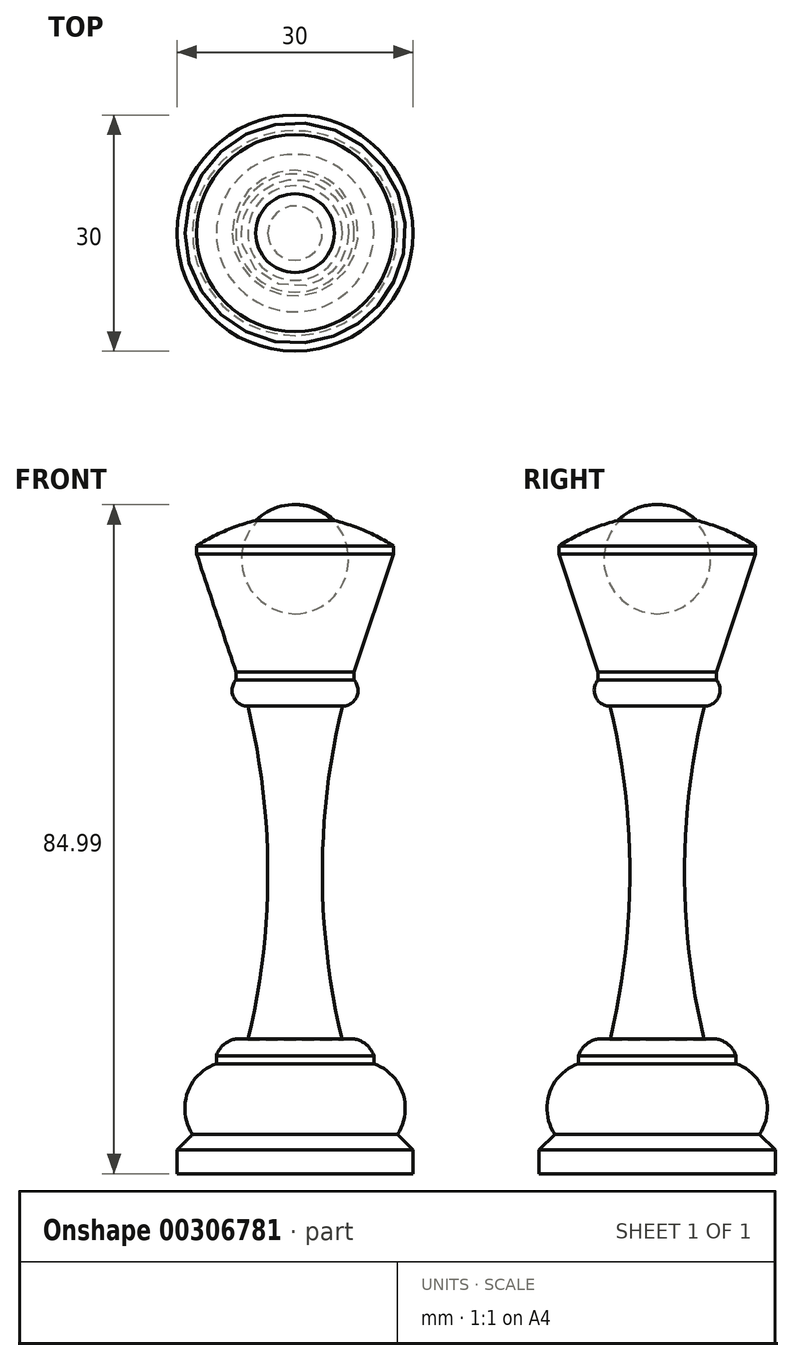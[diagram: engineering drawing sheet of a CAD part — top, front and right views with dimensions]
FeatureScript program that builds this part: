
annotation { "Feature Type Name" : "Feature", "Feature Type Description" : "" }
export const myFeature = defineFeature(function(context is Context, id is Id, definition is map)
    precondition{}
    {
        {
            var Q0;
            Q0=qCreatedBy(makeId("Front.planeOp"),FACE);
            var sketch = newSketch(context, id + "F0", { "sketchPlane" : qUnion([Q0])});
            skArc(sketch, "E0", {"start": v(12.5, -5.27) * mm, "mid": v(8.88, -3.33) * mm, "end": v(5, -2) * mm});
            skLineSegment(sketch, "E1", {"start": v(12.5, -5.27) * mm, "end": v(12.5, -6.27) * mm});
            skArc(sketch, "E2", {"start": v(6, -25.6) * mm, "mid": v(7.82, -24.41) * mm, "end": v(7.5, -22.27) * mm});
            skArc(sketch, "E3", {"start": v(6, -25.6) * mm, "mid": v(3.46, -46.8) * mm, "end": v(6, -68.02) * mm});
            skArc(sketch, "E4", {"start": v(13, -80) * mm, "mid": v(13.7, -74.77) * mm, "end": v(10, -71.02) * mm});
            skLineSegment(sketch, "E5", {"start": v(15, -82) * mm, "end": v(13, -80) * mm});
            skLineSegment(sketch, "E6", {"start": v(15, -82) * mm, "end": v(15, -85) * mm});
            skLineSegment(sketch, "E7", {"start": v(15, -84.99) * mm, "end": v(0, -84.99) * mm});
            skLineSegment(sketch, "E8", {"start": v(0, -84.99) * mm, "end": v(0, 0) * mm});
            skLineSegment(sketch, "E9", {"start": v(12.5, -6.27) * mm, "end": v(0, -6.27) * mm});
            skLineSegment(sketch, "E10", {"start": v(12.5, -5.27) * mm, "end": v(0, -5.27) * mm});
            skLineSegment(sketch, "E11", {"start": v(7.5, -22.27) * mm, "end": v(0, -22.27) * mm});
            skArc(sketch, "E12", {"start": v(5, -2) * mm, "mid": v(2.7, -0.5) * mm, "end": v(0, 0) * mm});
            skLineSegment(sketch, "E13", {"start": v(6, -25.6) * mm, "end": v(0, -25.6) * mm});
            skLineSegment(sketch, "E14", {"start": v(6, -68.02) * mm, "end": v(0, -68.02) * mm});
            skLineSegment(sketch, "E15", {"start": v(10, -71.02) * mm, "end": v(0, -71.02) * mm});
            skLineSegment(sketch, "E16", {"start": v(10, -70.02) * mm, "end": v(0, -70.02) * mm});
            skLineSegment(sketch, "E17", {"start": v(13, -79.99) * mm, "end": v(0, -79.99) * mm});
            skLineSegment(sketch, "E18", {"start": v(15, -81.99) * mm, "end": v(0, -81.99) * mm});
            skLineSegment(sketch, "E19", {"start": v(7.5, -21.27) * mm, "end": v(0, -21.27) * mm});
            skLineSegment(sketch, "E20", {"start": v(12.5, -6.27) * mm, "end": v(7.5, -21.27) * mm});
            skLineSegment(sketch, "E21", {"start": v(7.5, -22.27) * mm, "end": v(7.5, -21.27) * mm});
            skLineSegment(sketch, "E22", {"start": v(10, -71.02) * mm, "end": v(10, -70.02) * mm});
            skArc(sketch, "E23", {"start": v(10, -70.02) * mm, "mid": v(8.42, -68.18) * mm, "end": v(6, -68.02) * mm});
            skSolve(sketch);
        }
        {
            var Q0;
            Q0 = qSketchRegion(id + "F0", true);
            var Q1;
            Q1=sQuery(id+"F0.wireOp",EDGE,"E8");
            revolve(context, id + "F1", {"entities" : qUnion([Q0]), "axis" : qUnion([Q1]), "revolveType" : RevolveType.FULL});
        }
    });
